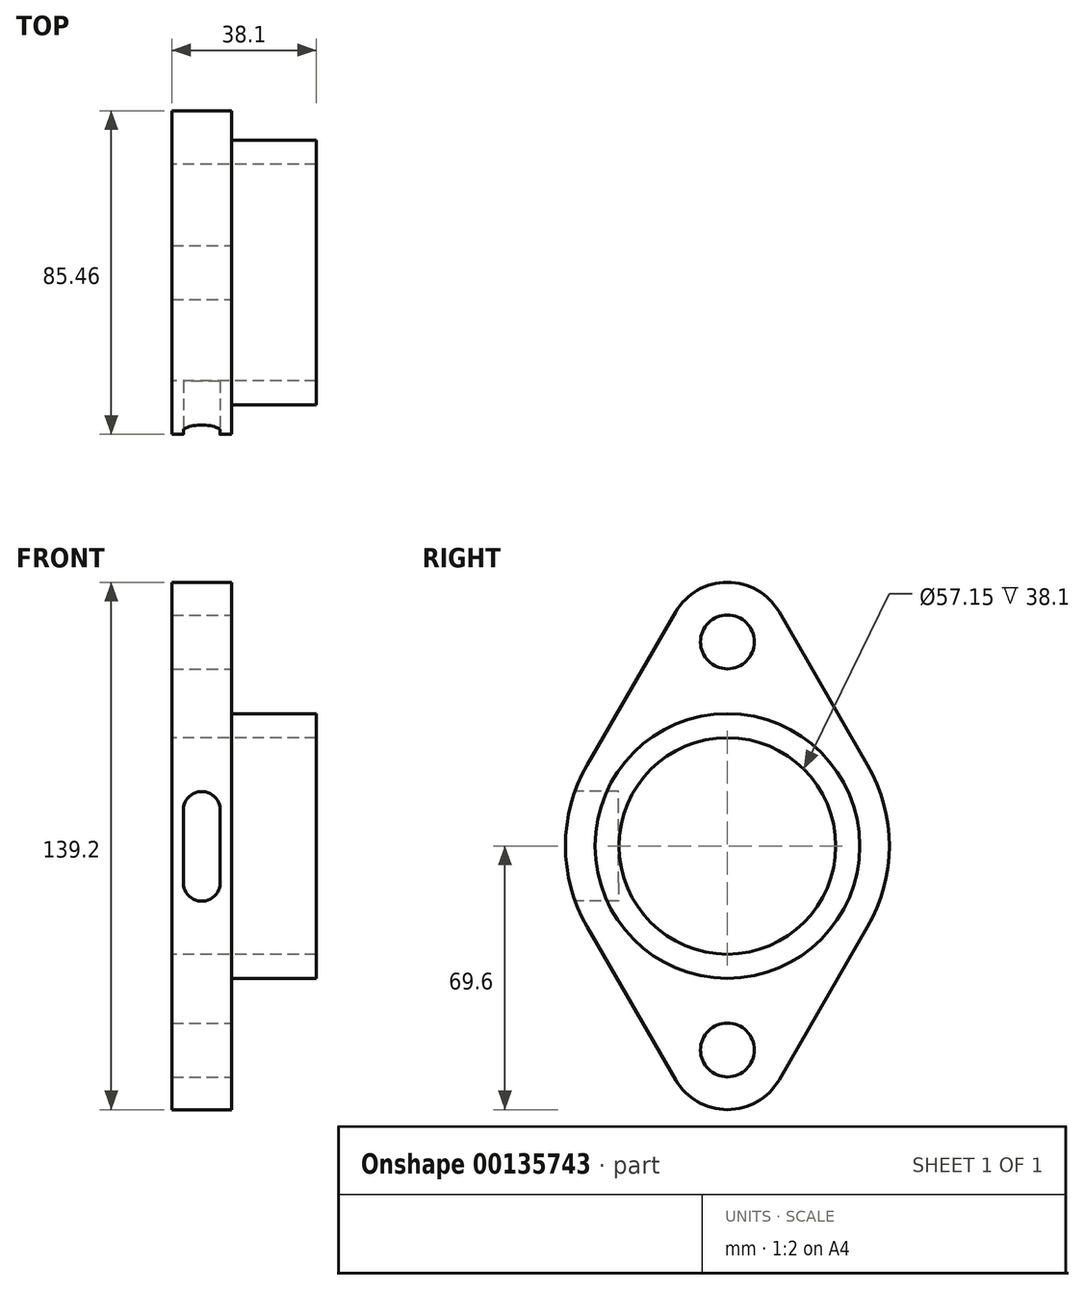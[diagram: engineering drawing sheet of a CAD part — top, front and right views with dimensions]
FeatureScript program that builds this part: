
annotation { "Feature Type Name" : "Feature", "Feature Type Description" : "" }
export const myFeature = defineFeature(function(context is Context, id is Id, definition is map)
    precondition{}
    {
        {
            var Q0;
            Q0=qCreatedBy(makeId("Right.planeOp"),FACE);
            var sketch = newSketch(context, id + "F0", { "sketchPlane" : qUnion([Q0])});
            skCircle(sketch, "E0", {"center": v(0, 0) * mm, "radius": 34.93 * mm});
            skCircle(sketch, "E1", {"center": v(0, 0) * mm, "radius": 28.58 * mm});
            skSolve(sketch);
        }
        {
            var Q0;
            Q0=makeQuery(id+"F0.imprint","IMPRINT",FACE,{"disambiguationData":[TD([[makeQuery(id+"F0.imprint","IMPRINT",EDGE,{"derivedFrom":sQuery(id+"F0.wireOp",EDGE,"E0")}),1.0]])]});
            extrude(context, id + "F1", {"entities" : qUnion([Q0]), "depth" : 22.35 * mm});
        }
        {
            var Q0;
            Q0=qCreatedBy(makeId("Right.planeOp"),FACE);
            var sketch = newSketch(context, id + "F2", { "sketchPlane" : qUnion([Q0])});
            skLineSegment(sketch, "E2", {"start": v(36.98, 21.41) * mm, "end": v(13.63, 61.74) * mm});
            skArc(sketch, "E3", {"start": v(13.63, 61.74) * mm, "mid": v(0, 69.6) * mm, "end": v(-13.63, 61.74) * mm});
            skLineSegment(sketch, "E4", {"start": v(-13.63, 61.74) * mm, "end": v(-36.98, 21.41) * mm});
            skLineSegment(sketch, "E5", {"start": v(36.98, -21.41) * mm, "end": v(13.63, -61.74) * mm});
            skArc(sketch, "E6", {"start": v(-13.63, -61.74) * mm, "mid": v(0, -69.6) * mm, "end": v(13.63, -61.74) * mm});
            skLineSegment(sketch, "E7", {"start": v(-13.63, -61.74) * mm, "end": v(-36.98, -21.41) * mm});
            skArc(sketch, "E8", {"start": v(36.98, 21.41) * mm, "mid": v(42.73, 0) * mm, "end": v(36.98, -21.41) * mm});
            skArc(sketch, "E9", {"start": v(-36.98, 21.41) * mm, "mid": v(-42.73, 0) * mm, "end": v(-36.98, -21.41) * mm});
            skCircle(sketch, "E10", {"center": v(0, -53.85) * mm, "radius": 7.11 * mm});
            skCircle(sketch, "E11", {"center": v(0, 53.85) * mm, "radius": 7.11 * mm});
            skSolve(sketch);
        }
        {
            var Q0;
            Q0=makeQuery(id+"F2.imprint","IMPRINT",FACE,{"disambiguationData":[TD([[makeQuery(id+"F2.imprint","IMPRINT",EDGE,{"derivedFrom":sQuery(id+"F2.wireOp",EDGE,"E2")}),1.0]])]});
            extrude(context, id + "F3", {"entities" : qUnion([Q0]), "operationType" : NewBodyOperationType.ADD, "oppositeDirection" : true, "depth" : 15.75 * mm});
        }
        {
            var Q0;
            Q0=qCreatedBy(makeId("Front.planeOp"),FACE);
            cPlane(context, id + "F4", {"entities" : qUnion([Q0]), "cplaneType" : CPlaneType.OFFSET, "offset" : 42.93 * mm, "width" : 152.4 * mm, "height" : 152.4 * mm});
        }
        {
            var Q0;
            Q0=qCreatedBy(id+"F4.planeOp",FACE);
            var sketch = newSketch(context, id + "F5", { "sketchPlane" : qUnion([Q0])});
            skLineSegment(sketch, "E12", {"start": v(-12.7, -9.76) * mm, "end": v(-12.7, 9.55) * mm});
            skLineSegment(sketch, "E13", {"start": v(-3.05, -9.76) * mm, "end": v(-3.05, 9.55) * mm});
            skArc(sketch, "E14", {"start": v(-3.05, 9.55) * mm, "mid": v(-7.87, 14.37) * mm, "end": v(-12.7, 9.55) * mm});
            skArc(sketch, "E15", {"start": v(-12.7, -9.76) * mm, "mid": v(-7.87, -14.58) * mm, "end": v(-3.05, -9.76) * mm});
            skLineSegment(sketch, "E16.0", {"start": v(0, 21.41) * mm, "end": v(0, -21.41) * mm});
            skLineSegment(sketch, "E16.1", {"start": v(-15.75, 21.41) * mm, "end": v(-15.75, -21.41) * mm});
            skSolve(sketch);
        }
        {
            var Q0;
            Q0=makeQuery(id+"F5.imprint","IMPRINT",FACE,{"disambiguationData":[TD([[makeQuery(id+"F5.imprint","IMPRINT",EDGE,{"derivedFrom":sQuery(id+"F5.wireOp",EDGE,"E12")}),-1.0]])]});
            extrude(context, id + "F6", {"entities" : qUnion([Q0]), "operationType" : NewBodyOperationType.REMOVE, "oppositeDirection" : true, "depth" : 14.22 * mm});
        }
        {
            var Q0;
            Q0=makeQuery(id+"F3.boolean.opBoolean","SPLIT",FACE,{"disambiguationData":[TD([makeQuery(id+"F1.opExtrude","SWEPT_FACE",FACE,{"disambiguationData":[OSD([sQuery(id+"F0.wireOp",EDGE,"E1")])]})])],"derivedFrom":makeQuery(id+"F3.opExtrude","CAP_FACE",FACE,{"disambiguationData":[OSD([sQuery(id+"F2.wireOp",EDGE,"E2"),sQuery(id+"F2.wireOp",EDGE,"E3"),sQuery(id+"F2.wireOp",EDGE,"E4"),sQuery(id+"F2.wireOp",EDGE,"E5"),sQuery(id+"F2.wireOp",EDGE,"E6"),sQuery(id+"F2.wireOp",EDGE,"E7"),sQuery(id+"F2.wireOp",EDGE,"E8"),sQuery(id+"F2.wireOp",EDGE,"E9"),sQuery(id+"F2.wireOp",EDGE,"E10"),sQuery(id+"F2.wireOp",EDGE,"E11")])],"isStart":true})});
            var sketch = newSketch(context, id + "F7", { "sketchPlane" : qUnion([Q0])});
            skCircle(sketch, "E17", {"center": v(0, 0) * mm, "radius": 28.58 * mm});
            skSolve(sketch);
        }
        {
            var Q0;
            Q0=makeQuery(id+"F7.imprint","IMPRINT",FACE,{"disambiguationData":[TD([[makeQuery(id+"F7.imprint","IMPRINT",EDGE,{"derivedFrom":sQuery(id+"F7.wireOp",EDGE,"E17")}),1.0]])]});
            extrude(context, id + "F8", {"entities" : qUnion([Q0]), "operationType" : NewBodyOperationType.REMOVE, "endBound" : BoundingType.THROUGH_ALL, "oppositeDirection" : true, "depth" : 25.4 * mm});
        }
    });
